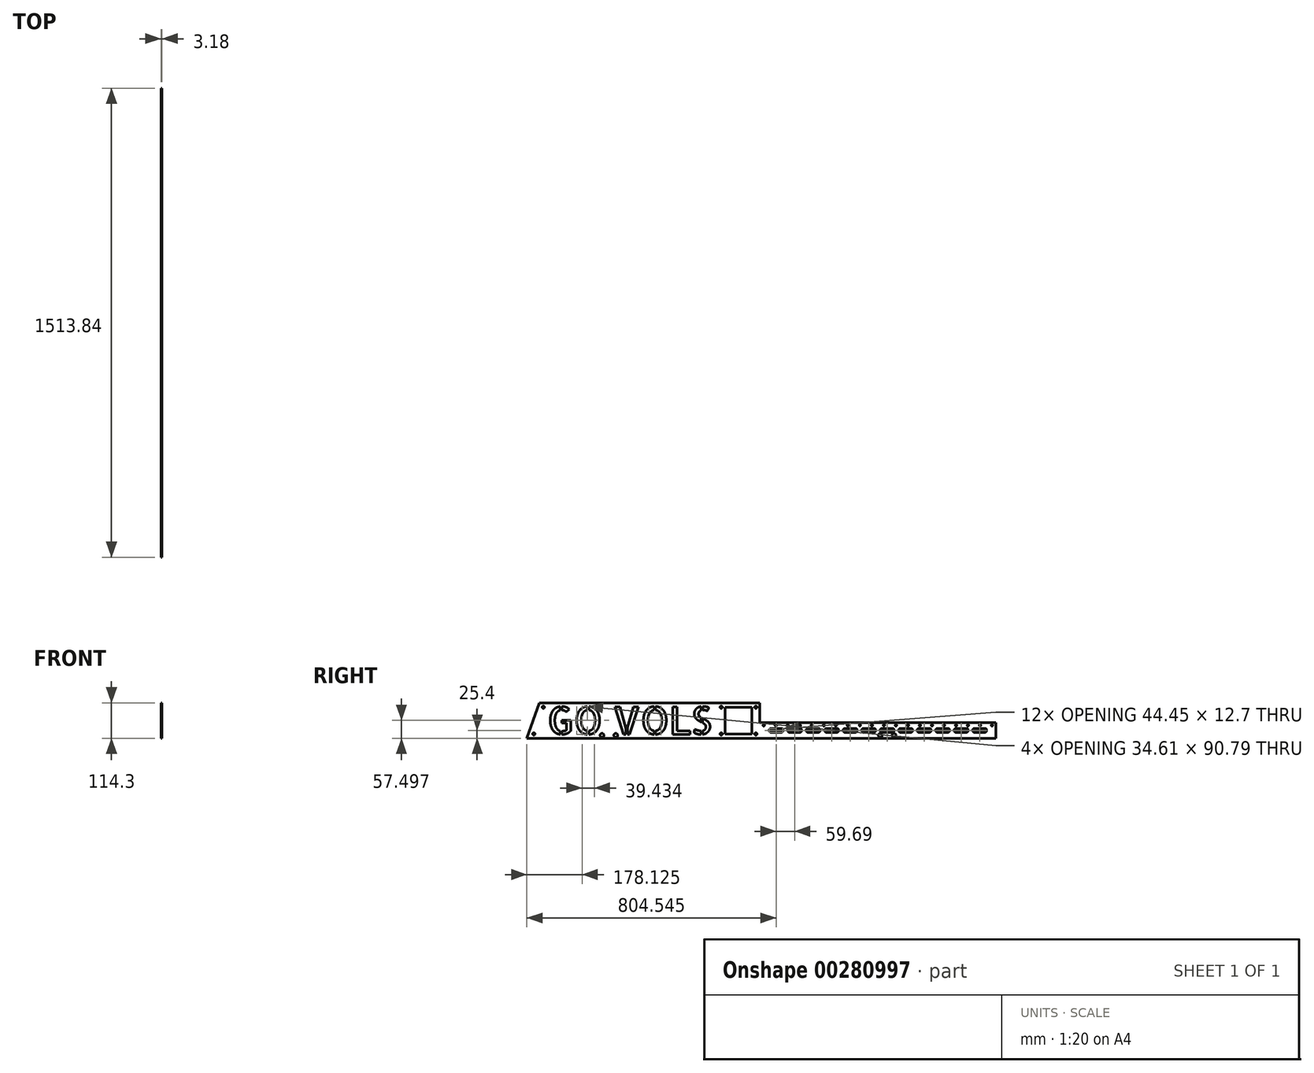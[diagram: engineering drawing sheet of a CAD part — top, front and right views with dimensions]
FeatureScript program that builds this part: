
annotation { "Feature Type Name" : "Feature", "Feature Type Description" : "" }
export const myFeature = defineFeature(function(context is Context, id is Id, definition is map)
    precondition{}
    {
        {
            var Q0;
            Q0=qCreatedBy(makeId("Right.planeOp"),FACE);
            var sketch = newSketch(context, id + "F0", { "sketchPlane" : qUnion([Q0])});
            skLineSegment(sketch, "E0", {"start": v(0, 0) * mm, "end": v(40.64, 114.3) * mm});
            skLineSegment(sketch, "E1", {"start": v(40.64, 114.3) * mm, "end": v(751.84, 114.3) * mm});
            skLineSegment(sketch, "E2", {"start": v(751.84, 114.3) * mm, "end": v(751.84, 50.8) * mm});
            skLineSegment(sketch, "E3", {"start": v(751.84, 50.8) * mm, "end": v(1513.84, 50.8) * mm});
            skLineSegment(sketch, "E4", {"start": v(1513.84, 50.8) * mm, "end": v(1513.84, 0) * mm});
            skLineSegment(sketch, "E5", {"start": v(1513.84, 0) * mm, "end": v(0, 0) * mm});
            skSolve(sketch);
        }
        {
            var Q0;
            Q0 = qSketchRegion(id + "F0", true);
            extrude(context, id + "F1", {"entities" : qUnion([Q0]), "oppositeDirection" : true, "depth" : 3.17 * mm});
        }
        {
            var Q0;
            Q0=makeQuery(id+"F1.opExtrude","CAP_FACE",FACE,{"disambiguationData":[OSD([sQuery(id+"F0.wireOp",EDGE,"E0"),sQuery(id+"F0.wireOp",EDGE,"E1"),sQuery(id+"F0.wireOp",EDGE,"E2"),sQuery(id+"F0.wireOp",EDGE,"E3"),sQuery(id+"F0.wireOp",EDGE,"E4"),sQuery(id+"F0.wireOp",EDGE,"E5")])],"isStart":true});
            var sketch = newSketch(context, id + "F2", { "sketchPlane" : qUnion([Q0])});
            skText(sketch, "E6", { "text": "GO VOLS", "fontName": "AllertaStencil-Regular.ttf"});
            skLineSegment(sketch, "E7.bottom", {"start": v(726.44, 13.97) * mm, "end": v(640.08, 13.97) * mm});
            skLineSegment(sketch, "E7.top", {"start": v(726.44, 100.33) * mm, "end": v(640.08, 100.33) * mm});
            skLineSegment(sketch, "E7.left", {"start": v(726.44, 13.97) * mm, "end": v(726.44, 100.33) * mm});
            skLineSegment(sketch, "E7.right", {"start": v(640.08, 13.97) * mm, "end": v(640.08, 100.33) * mm});
            skPoint(sketch, "E7.middle", {"position": v(683.26, 57.15) * mm});
            const initialGuessF2  = {"E6": [0.06592, 0.0127, 1, 0, 0.0889]};
            skSetInitialGuess(sketch, initialGuessF2);
            skSolve(sketch);
        }
        {
            var Q0;
            Q0 = qSketchRegion(id + "F2", true);
            var Q1;
            Q1=makeQuery(id+"F1.opExtrude","CAP_FACE",FACE,{"disambiguationData":[OSD([sQuery(id+"F0.wireOp",EDGE,"E0"),sQuery(id+"F0.wireOp",EDGE,"E1"),sQuery(id+"F0.wireOp",EDGE,"E2"),sQuery(id+"F0.wireOp",EDGE,"E3"),sQuery(id+"F0.wireOp",EDGE,"E4"),sQuery(id+"F0.wireOp",EDGE,"E5")])],"isStart":false});
            extrude(context, id + "F3", {"entities" : qUnion([Q0]), "operationType" : NewBodyOperationType.REMOVE, "endBound" : BoundingType.UP_TO_SURFACE, "oppositeDirection" : true, "endBoundEntityFace" : qUnion([Q1]), "depth" : 25.4 * mm});
        }
        {
            var Q0;
            Q0=makeQuery(id+"F1.opExtrude","CAP_FACE",FACE,{"disambiguationData":[OSD([sQuery(id+"F0.wireOp",EDGE,"E0"),sQuery(id+"F0.wireOp",EDGE,"E1"),sQuery(id+"F0.wireOp",EDGE,"E2"),sQuery(id+"F0.wireOp",EDGE,"E3"),sQuery(id+"F0.wireOp",EDGE,"E4"),sQuery(id+"F0.wireOp",EDGE,"E5")])],"isStart":true});
            var sketch = newSketch(context, id + "F4", { "sketchPlane" : qUnion([Q0])});
            skLineSegment(sketch, "E8", {"start": v(683.26, 100.33) * mm, "end": v(683.26, 63.34) * mm, "construction": true});
            skPoint(sketch, "E8.endSnap0", {"position": v(683.26, 100.33) * mm});
            skLineSegment(sketch, "E9", {"start": v(640.08, 57.15) * mm, "end": v(671.5, 57.15) * mm, "construction": true});
            skLineSegment(sketch, "E10", {"start": v(640.08, 100.33) * mm, "end": v(-159.31, 100.33) * mm, "construction": true});
            skCircle(sketch, "E11", {"center": v(739.14, 100.33) * mm, "radius": 3.81 * mm});
            skCircle(sketch, "E12.MirrorC", {"center": v(627.38, 100.33) * mm, "radius": 3.81 * mm});
            skCircle(sketch, "E13.MirrorC", {"center": v(627.38, 13.97) * mm, "radius": 3.81 * mm});
            skCircle(sketch, "E14.MirrorC", {"center": v(739.14, 13.97) * mm, "radius": 3.81 * mm});
            skCircle(sketch, "E15", {"center": v(53.34, 100.33) * mm, "radius": 3.81 * mm});
            skLineSegment(sketch, "E16", {"start": v(640.08, 13.97) * mm, "end": v(0, 13.97) * mm, "construction": true});
            skCircle(sketch, "E17", {"center": v(22.63, 13.97) * mm, "radius": 3.81 * mm});
            skLineSegment(sketch, "E18", {"start": v(53.34, 100.33) * mm, "end": v(8.36, -26.17) * mm, "construction": true});
            skCircle(sketch, "E19", {"center": v(242.57, 9.4) * mm, "radius": 6.35 * mm});
            skCircle(sketch, "E20", {"center": v(287.02, 9.4) * mm, "radius": 6.35 * mm});
            skLineSegment(sketch, "E21", {"start": v(287.02, 9.4) * mm, "end": v(1660.47, 9.4) * mm, "construction": true});
            skCircle(sketch, "E22", {"center": v(1140.46, 9.4) * mm, "radius": 6.35 * mm});
            skCircle(sketch, "E23", {"center": v(1184.9, 9.4) * mm, "radius": 6.35 * mm});
            skLineSegment(sketch, "E24", {"start": v(1513.84, 25.4) * mm, "end": v(751.84, 25.4) * mm, "construction": true});
            skLineSegment(sketch, "E25.bottom", {"start": v(821.7, 31.75) * mm, "end": v(787.4, 31.75) * mm});
            skLineSegment(sketch, "E25.top", {"start": v(821.7, 19.05) * mm, "end": v(787.4, 19.05) * mm});
            skLineSegment(sketch, "E25.left", {"start": v(826.77, 26.67) * mm, "end": v(826.77, 24.13) * mm});
            skLineSegment(sketch, "E25.right", {"start": v(782.32, 26.67) * mm, "end": v(782.32, 24.13) * mm});
            skPoint(sketch, "E25.middle", {"position": v(804.54, 25.4) * mm});
            skPoint(sketch, "E26.visualSharp", {"position": v(826.77, 31.75) * mm});
            skArc(sketch, "E26.filletArc", {"start": v(826.77, 26.67) * mm, "mid": v(825.28, 30.26) * mm, "end": v(821.7, 31.75) * mm});
            skPoint(sketch, "E27.visualSharp", {"position": v(782.32, 31.75) * mm});
            skArc(sketch, "E27.filletArc", {"start": v(787.4, 31.75) * mm, "mid": v(783.8, 30.26) * mm, "end": v(782.32, 26.67) * mm});
            skPoint(sketch, "E28.visualSharp", {"position": v(782.32, 19.05) * mm});
            skArc(sketch, "E28.filletArc", {"start": v(782.32, 24.13) * mm, "mid": v(783.8, 20.54) * mm, "end": v(787.4, 19.05) * mm});
            skPoint(sketch, "E29.visualSharp", {"position": v(826.77, 19.05) * mm});
            skArc(sketch, "E29.filletArc", {"start": v(821.7, 19.05) * mm, "mid": v(825.28, 20.54) * mm, "end": v(826.77, 24.13) * mm});
            skLineSegment(sketch, "E30.1.0.0", {"start": v(842, 26.67) * mm, "end": v(842, 24.13) * mm});
            skLineSegment(sketch, "E30.1.0.1", {"start": v(886.46, 26.67) * mm, "end": v(886.46, 24.13) * mm});
            skLineSegment(sketch, "E30.1.0.2", {"start": v(881.38, 31.75) * mm, "end": v(847.09, 31.75) * mm});
            skArc(sketch, "E30.1.0.3", {"start": v(842, 24.13) * mm, "mid": v(843.5, 20.54) * mm, "end": v(847.09, 19.05) * mm});
            skArc(sketch, "E30.1.0.4", {"start": v(886.46, 26.67) * mm, "mid": v(884.97, 30.26) * mm, "end": v(881.38, 31.75) * mm});
            skArc(sketch, "E30.1.0.5", {"start": v(881.38, 19.05) * mm, "mid": v(884.97, 20.54) * mm, "end": v(886.46, 24.13) * mm});
            skLineSegment(sketch, "E30.1.0.6", {"start": v(881.38, 19.05) * mm, "end": v(847.09, 19.05) * mm});
            skArc(sketch, "E30.1.0.7", {"start": v(847.09, 31.75) * mm, "mid": v(843.5, 30.26) * mm, "end": v(842, 26.67) * mm});
            skLineSegment(sketch, "E30.2.0.0", {"start": v(901.7, 26.67) * mm, "end": v(901.7, 24.13) * mm});
            skLineSegment(sketch, "E30.2.0.1", {"start": v(946.15, 26.67) * mm, "end": v(946.15, 24.13) * mm});
            skLineSegment(sketch, "E30.2.0.2", {"start": v(941.07, 31.75) * mm, "end": v(906.78, 31.75) * mm});
            skArc(sketch, "E30.2.0.3", {"start": v(901.7, 24.13) * mm, "mid": v(903.19, 20.54) * mm, "end": v(906.78, 19.05) * mm});
            skArc(sketch, "E30.2.0.4", {"start": v(946.15, 26.67) * mm, "mid": v(944.66, 30.26) * mm, "end": v(941.07, 31.75) * mm});
            skArc(sketch, "E30.2.0.5", {"start": v(941.07, 19.05) * mm, "mid": v(944.66, 20.54) * mm, "end": v(946.15, 24.13) * mm});
            skLineSegment(sketch, "E30.2.0.6", {"start": v(941.07, 19.05) * mm, "end": v(906.78, 19.05) * mm});
            skArc(sketch, "E30.2.0.7", {"start": v(906.78, 31.75) * mm, "mid": v(903.19, 30.26) * mm, "end": v(901.7, 26.67) * mm});
            skLineSegment(sketch, "E30.3.0.0", {"start": v(961.39, 26.67) * mm, "end": v(961.39, 24.13) * mm});
            skLineSegment(sketch, "E30.3.0.1", {"start": v(1005.84, 26.67) * mm, "end": v(1005.84, 24.13) * mm});
            skLineSegment(sketch, "E30.3.0.2", {"start": v(1000.76, 31.75) * mm, "end": v(966.47, 31.75) * mm});
            skArc(sketch, "E30.3.0.3", {"start": v(961.39, 24.13) * mm, "mid": v(962.88, 20.54) * mm, "end": v(966.47, 19.05) * mm});
            skArc(sketch, "E30.3.0.4", {"start": v(1005.84, 26.67) * mm, "mid": v(1004.35, 30.26) * mm, "end": v(1000.76, 31.75) * mm});
            skArc(sketch, "E30.3.0.5", {"start": v(1000.76, 19.05) * mm, "mid": v(1004.35, 20.54) * mm, "end": v(1005.84, 24.13) * mm});
            skLineSegment(sketch, "E30.3.0.6", {"start": v(1000.76, 19.05) * mm, "end": v(966.47, 19.05) * mm});
            skArc(sketch, "E30.3.0.7", {"start": v(966.47, 31.75) * mm, "mid": v(962.88, 30.26) * mm, "end": v(961.39, 26.67) * mm});
            skLineSegment(sketch, "E30.4.0.0", {"start": v(1021.08, 26.67) * mm, "end": v(1021.08, 24.13) * mm});
            skLineSegment(sketch, "E30.4.0.1", {"start": v(1065.53, 26.67) * mm, "end": v(1065.53, 24.13) * mm});
            skLineSegment(sketch, "E30.4.0.2", {"start": v(1060.45, 31.75) * mm, "end": v(1026.16, 31.75) * mm});
            skArc(sketch, "E30.4.0.3", {"start": v(1021.08, 24.13) * mm, "mid": v(1022.57, 20.54) * mm, "end": v(1026.16, 19.05) * mm});
            skArc(sketch, "E30.4.0.4", {"start": v(1065.53, 26.67) * mm, "mid": v(1064.04, 30.26) * mm, "end": v(1060.45, 31.75) * mm});
            skArc(sketch, "E30.4.0.5", {"start": v(1060.45, 19.05) * mm, "mid": v(1064.04, 20.54) * mm, "end": v(1065.53, 24.13) * mm});
            skLineSegment(sketch, "E30.4.0.6", {"start": v(1060.45, 19.05) * mm, "end": v(1026.16, 19.05) * mm});
            skArc(sketch, "E30.4.0.7", {"start": v(1026.16, 31.75) * mm, "mid": v(1022.57, 30.26) * mm, "end": v(1021.08, 26.67) * mm});
            skLineSegment(sketch, "E30.5.0.0", {"start": v(1080.77, 26.67) * mm, "end": v(1080.77, 24.13) * mm});
            skLineSegment(sketch, "E30.5.0.1", {"start": v(1125.22, 26.67) * mm, "end": v(1125.22, 24.13) * mm});
            skLineSegment(sketch, "E30.5.0.2", {"start": v(1120.14, 31.75) * mm, "end": v(1085.85, 31.75) * mm});
            skArc(sketch, "E30.5.0.3", {"start": v(1080.77, 24.13) * mm, "mid": v(1082.26, 20.54) * mm, "end": v(1085.85, 19.05) * mm});
            skArc(sketch, "E30.5.0.4", {"start": v(1125.22, 26.67) * mm, "mid": v(1123.73, 30.26) * mm, "end": v(1120.14, 31.75) * mm});
            skArc(sketch, "E30.5.0.5", {"start": v(1120.14, 19.05) * mm, "mid": v(1123.73, 20.54) * mm, "end": v(1125.22, 24.13) * mm});
            skLineSegment(sketch, "E30.5.0.6", {"start": v(1120.14, 19.05) * mm, "end": v(1085.85, 19.05) * mm});
            skArc(sketch, "E30.5.0.7", {"start": v(1085.85, 31.75) * mm, "mid": v(1082.26, 30.26) * mm, "end": v(1080.77, 26.67) * mm});
            skLineSegment(sketch, "E30.6.0.0", {"start": v(1140.46, 26.67) * mm, "end": v(1140.46, 24.13) * mm});
            skLineSegment(sketch, "E30.6.0.1", {"start": v(1184.9, 26.67) * mm, "end": v(1184.9, 24.13) * mm});
            skLineSegment(sketch, "E30.6.0.2", {"start": v(1179.83, 31.75) * mm, "end": v(1145.54, 31.75) * mm});
            skArc(sketch, "E30.6.0.3", {"start": v(1140.46, 24.13) * mm, "mid": v(1141.95, 20.54) * mm, "end": v(1145.54, 19.05) * mm});
            skArc(sketch, "E30.6.0.4", {"start": v(1184.9, 26.67) * mm, "mid": v(1183.42, 30.26) * mm, "end": v(1179.83, 31.75) * mm});
            skArc(sketch, "E30.6.0.5", {"start": v(1179.83, 19.05) * mm, "mid": v(1183.42, 20.54) * mm, "end": v(1184.9, 24.13) * mm});
            skLineSegment(sketch, "E30.6.0.6", {"start": v(1179.83, 19.05) * mm, "end": v(1145.54, 19.05) * mm});
            skArc(sketch, "E30.6.0.7", {"start": v(1145.54, 31.75) * mm, "mid": v(1141.95, 30.26) * mm, "end": v(1140.46, 26.67) * mm});
            skLineSegment(sketch, "E30.7.0.0", {"start": v(1200.15, 26.67) * mm, "end": v(1200.15, 24.13) * mm});
            skLineSegment(sketch, "E30.7.0.1", {"start": v(1244.6, 26.67) * mm, "end": v(1244.6, 24.13) * mm});
            skLineSegment(sketch, "E30.7.0.2", {"start": v(1239.52, 31.75) * mm, "end": v(1205.23, 31.75) * mm});
            skArc(sketch, "E30.7.0.3", {"start": v(1200.15, 24.13) * mm, "mid": v(1201.64, 20.54) * mm, "end": v(1205.23, 19.05) * mm});
            skArc(sketch, "E30.7.0.4", {"start": v(1244.6, 26.67) * mm, "mid": v(1243.11, 30.26) * mm, "end": v(1239.52, 31.75) * mm});
            skArc(sketch, "E30.7.0.5", {"start": v(1239.52, 19.05) * mm, "mid": v(1243.11, 20.54) * mm, "end": v(1244.6, 24.13) * mm});
            skLineSegment(sketch, "E30.7.0.6", {"start": v(1239.52, 19.05) * mm, "end": v(1205.23, 19.05) * mm});
            skArc(sketch, "E30.7.0.7", {"start": v(1205.23, 31.75) * mm, "mid": v(1201.64, 30.26) * mm, "end": v(1200.15, 26.67) * mm});
            skLineSegment(sketch, "E30.8.0.0", {"start": v(1259.84, 26.67) * mm, "end": v(1259.84, 24.13) * mm});
            skLineSegment(sketch, "E30.8.0.1", {"start": v(1304.29, 26.67) * mm, "end": v(1304.29, 24.13) * mm});
            skLineSegment(sketch, "E30.8.0.2", {"start": v(1299.2, 31.75) * mm, "end": v(1264.92, 31.75) * mm});
            skArc(sketch, "E30.8.0.3", {"start": v(1259.84, 24.13) * mm, "mid": v(1261.33, 20.54) * mm, "end": v(1264.92, 19.05) * mm});
            skArc(sketch, "E30.8.0.4", {"start": v(1304.29, 26.67) * mm, "mid": v(1302.8, 30.26) * mm, "end": v(1299.2, 31.75) * mm});
            skArc(sketch, "E30.8.0.5", {"start": v(1299.2, 19.05) * mm, "mid": v(1302.8, 20.54) * mm, "end": v(1304.29, 24.13) * mm});
            skLineSegment(sketch, "E30.8.0.6", {"start": v(1299.2, 19.05) * mm, "end": v(1264.92, 19.05) * mm});
            skArc(sketch, "E30.8.0.7", {"start": v(1264.92, 31.75) * mm, "mid": v(1261.33, 30.26) * mm, "end": v(1259.84, 26.67) * mm});
            skLineSegment(sketch, "E30.9.0.0", {"start": v(1319.53, 26.67) * mm, "end": v(1319.53, 24.13) * mm});
            skLineSegment(sketch, "E30.9.0.1", {"start": v(1363.98, 26.67) * mm, "end": v(1363.98, 24.13) * mm});
            skLineSegment(sketch, "E30.9.0.2", {"start": v(1358.9, 31.75) * mm, "end": v(1324.6, 31.75) * mm});
            skArc(sketch, "E30.9.0.3", {"start": v(1319.53, 24.13) * mm, "mid": v(1321.02, 20.54) * mm, "end": v(1324.6, 19.05) * mm});
            skArc(sketch, "E30.9.0.4", {"start": v(1363.98, 26.67) * mm, "mid": v(1362.5, 30.26) * mm, "end": v(1358.9, 31.75) * mm});
            skArc(sketch, "E30.9.0.5", {"start": v(1358.9, 19.05) * mm, "mid": v(1362.5, 20.54) * mm, "end": v(1363.98, 24.13) * mm});
            skLineSegment(sketch, "E30.9.0.6", {"start": v(1358.9, 19.05) * mm, "end": v(1324.6, 19.05) * mm});
            skArc(sketch, "E30.9.0.7", {"start": v(1324.6, 31.75) * mm, "mid": v(1321.02, 30.26) * mm, "end": v(1319.53, 26.67) * mm});
            skLineSegment(sketch, "E30.10.0.0", {"start": v(1379.22, 26.67) * mm, "end": v(1379.22, 24.13) * mm});
            skLineSegment(sketch, "E30.10.0.1", {"start": v(1423.67, 26.67) * mm, "end": v(1423.67, 24.13) * mm});
            skLineSegment(sketch, "E30.10.0.2", {"start": v(1418.59, 31.75) * mm, "end": v(1384.3, 31.75) * mm});
            skArc(sketch, "E30.10.0.3", {"start": v(1379.22, 24.13) * mm, "mid": v(1380.7, 20.54) * mm, "end": v(1384.3, 19.05) * mm});
            skArc(sketch, "E30.10.0.4", {"start": v(1423.67, 26.67) * mm, "mid": v(1422.18, 30.26) * mm, "end": v(1418.59, 31.75) * mm});
            skArc(sketch, "E30.10.0.5", {"start": v(1418.59, 19.05) * mm, "mid": v(1422.18, 20.54) * mm, "end": v(1423.67, 24.13) * mm});
            skLineSegment(sketch, "E30.10.0.6", {"start": v(1418.59, 19.05) * mm, "end": v(1384.3, 19.05) * mm});
            skArc(sketch, "E30.10.0.7", {"start": v(1384.3, 31.75) * mm, "mid": v(1380.7, 30.26) * mm, "end": v(1379.22, 26.67) * mm});
            skLineSegment(sketch, "E30.11.0.0", {"start": v(1438.9, 26.67) * mm, "end": v(1438.9, 24.13) * mm});
            skLineSegment(sketch, "E30.11.0.1", {"start": v(1483.36, 26.67) * mm, "end": v(1483.36, 24.13) * mm});
            skLineSegment(sketch, "E30.11.0.2", {"start": v(1478.28, 31.75) * mm, "end": v(1443.99, 31.75) * mm});
            skArc(sketch, "E30.11.0.3", {"start": v(1438.9, 24.13) * mm, "mid": v(1440.4, 20.54) * mm, "end": v(1443.99, 19.05) * mm});
            skArc(sketch, "E30.11.0.4", {"start": v(1483.36, 26.67) * mm, "mid": v(1481.87, 30.26) * mm, "end": v(1478.28, 31.75) * mm});
            skArc(sketch, "E30.11.0.5", {"start": v(1478.28, 19.05) * mm, "mid": v(1481.87, 20.54) * mm, "end": v(1483.36, 24.13) * mm});
            skLineSegment(sketch, "E30.11.0.6", {"start": v(1478.28, 19.05) * mm, "end": v(1443.99, 19.05) * mm});
            skArc(sketch, "E30.11.0.7", {"start": v(1443.99, 31.75) * mm, "mid": v(1440.4, 30.26) * mm, "end": v(1438.9, 26.67) * mm});
            skLineSegment(sketch, "E30.direction1", {"start": v(787.4, 31.75) * mm, "end": v(847.09, 31.75) * mm, "construction": true});
            skCircle(sketch, "E31", {"center": v(764.54, 41.91) * mm, "radius": 2.54 * mm});
            skCircle(sketch, "E32.1.0.0", {"center": v(803.3, 41.91) * mm, "radius": 2.54 * mm});
            skCircle(sketch, "E32.2.0.0", {"center": v(842.08, 41.91) * mm, "radius": 2.54 * mm});
            skCircle(sketch, "E32.3.0.0", {"center": v(880.84, 41.91) * mm, "radius": 2.54 * mm});
            skCircle(sketch, "E32.4.0.0", {"center": v(919.61, 41.91) * mm, "radius": 2.54 * mm});
            skCircle(sketch, "E32.5.0.0", {"center": v(958.38, 41.91) * mm, "radius": 2.54 * mm});
            skCircle(sketch, "E32.6.0.0", {"center": v(997.15, 41.91) * mm, "radius": 2.54 * mm});
            skCircle(sketch, "E32.7.0.0", {"center": v(1035.92, 41.91) * mm, "radius": 2.54 * mm});
            skCircle(sketch, "E32.8.0.0", {"center": v(1074.69, 41.91) * mm, "radius": 2.54 * mm});
            skCircle(sketch, "E32.9.0.0", {"center": v(1113.45, 41.91) * mm, "radius": 2.54 * mm});
            skCircle(sketch, "E32.10.0.0", {"center": v(1152.22, 41.91) * mm, "radius": 2.54 * mm});
            skCircle(sketch, "E32.11.0.0", {"center": v(1191, 41.91) * mm, "radius": 2.54 * mm});
            skCircle(sketch, "E32.12.0.0", {"center": v(1229.76, 41.91) * mm, "radius": 2.54 * mm});
            skCircle(sketch, "E32.13.0.0", {"center": v(1268.53, 41.91) * mm, "radius": 2.54 * mm});
            skCircle(sketch, "E32.14.0.0", {"center": v(1307.3, 41.91) * mm, "radius": 2.54 * mm});
            skCircle(sketch, "E32.15.0.0", {"center": v(1346.06, 41.91) * mm, "radius": 2.54 * mm});
            skCircle(sketch, "E32.16.0.0", {"center": v(1384.83, 41.91) * mm, "radius": 2.54 * mm});
            skCircle(sketch, "E32.17.0.0", {"center": v(1423.6, 41.91) * mm, "radius": 2.54 * mm});
            skCircle(sketch, "E32.18.0.0", {"center": v(1462.37, 41.91) * mm, "radius": 2.54 * mm});
            skCircle(sketch, "E32.19.0.0", {"center": v(1501.14, 41.91) * mm, "radius": 2.54 * mm});
            skLineSegment(sketch, "E32.direction1", {"start": v(764.54, 41.91) * mm, "end": v(803.3, 41.91) * mm, "construction": true});
            skSolve(sketch);
        }
        {
            var Q0;
            Q0 = qSketchRegion(id + "F4", true);
            var Q1;
            Q1=makeQuery(id+"F1.opExtrude","CAP_FACE",FACE,{"disambiguationData":[OSD([sQuery(id+"F0.wireOp",EDGE,"E0"),sQuery(id+"F0.wireOp",EDGE,"E1"),sQuery(id+"F0.wireOp",EDGE,"E2"),sQuery(id+"F0.wireOp",EDGE,"E3"),sQuery(id+"F0.wireOp",EDGE,"E4"),sQuery(id+"F0.wireOp",EDGE,"E5")])],"isStart":false});
            extrude(context, id + "F5", {"entities" : qUnion([Q0]), "operationType" : NewBodyOperationType.REMOVE, "endBound" : BoundingType.UP_TO_SURFACE, "oppositeDirection" : true, "endBoundEntityFace" : qUnion([Q1]), "depth" : 25.4 * mm});
        }
    });
